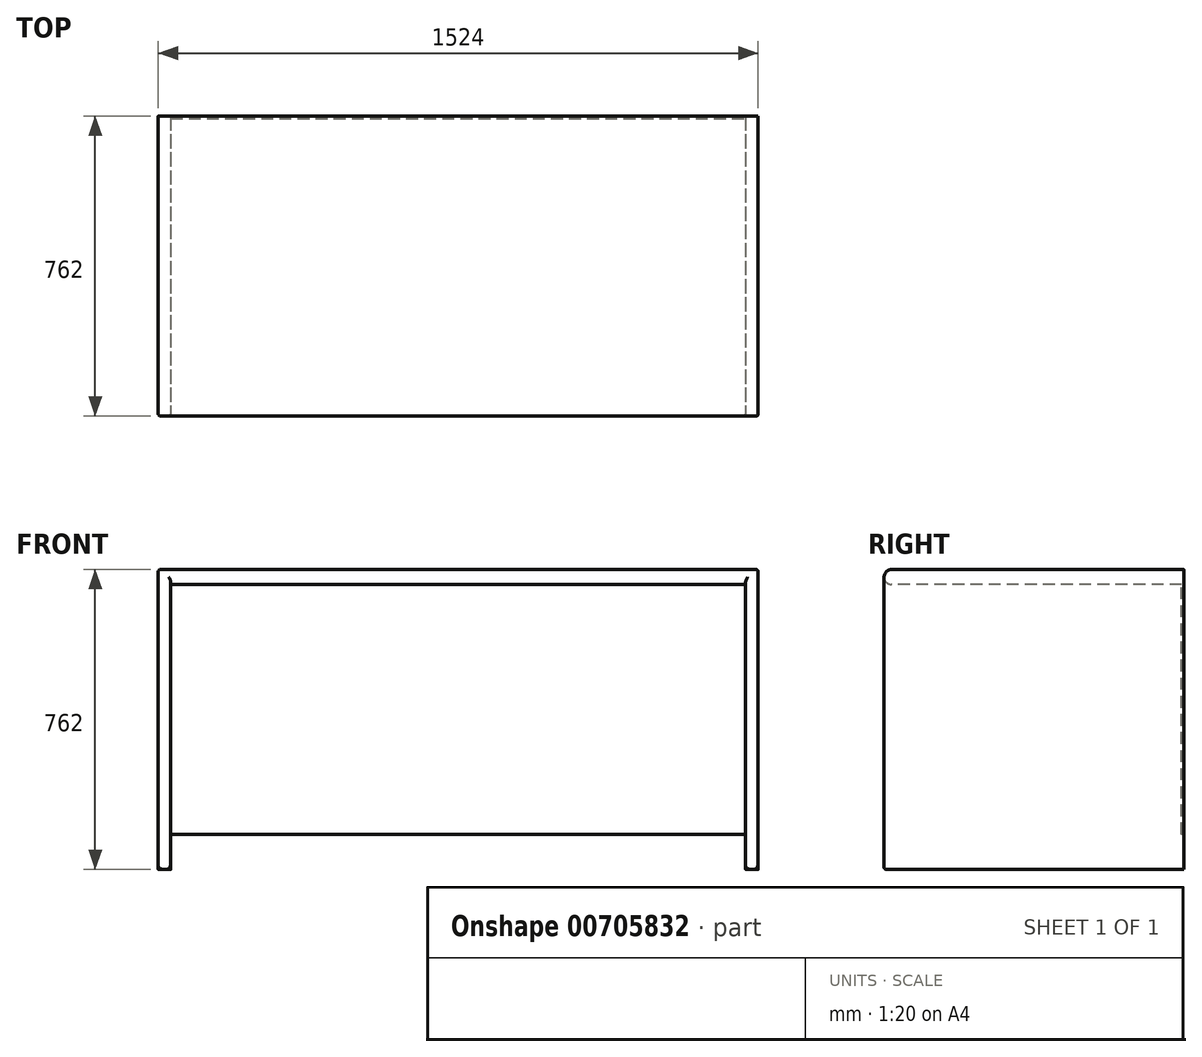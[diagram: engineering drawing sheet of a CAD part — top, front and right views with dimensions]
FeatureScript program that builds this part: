
annotation { "Feature Type Name" : "Feature", "Feature Type Description" : "" }
export const myFeature = defineFeature(function(context is Context, id is Id, definition is map)
    precondition{}
    {
        {
            var Q0;
            Q0=qCreatedBy(makeId("Top.planeOp"),FACE);
            var sketch = newSketch(context, id + "F0", { "sketchPlane" : qUnion([Q0])});
            skLineSegment(sketch, "E0.bottom", {"start": v(0, 0) * mm, "end": v(1524, 0) * mm});
            skLineSegment(sketch, "E0.top", {"start": v(0, 762) * mm, "end": v(1524, 762) * mm});
            skLineSegment(sketch, "E0.left", {"start": v(0, 0) * mm, "end": v(0, 762) * mm});
            skLineSegment(sketch, "E0.right", {"start": v(1524, 0) * mm, "end": v(1524, 762) * mm});
            skLineSegment(sketch, "E1", {"start": v(31.75, 762) * mm, "end": v(31.75, 0) * mm});
            skLineSegment(sketch, "E2", {"start": v(1492.25, 762) * mm, "end": v(1492.25, 0) * mm});
            skLineSegment(sketch, "E3", {"start": v(31.75, 755.65) * mm, "end": v(1492.25, 755.65) * mm});
            skSolve(sketch);
        }
        {
            var Q0;
            {var subQ5=sQuery(id+"F0.wireOp",EDGE,"E3");Q0=makeQuery(id+"F0.imprint","IMPRINT",FACE,{"disambiguationData":[TD([[makeQuery(id+"F0.imprint","IMPRINT",EDGE,{"derivedFrom":subQ5}),-1.0]])]});}
            var Q1;
            {var subQ0=sQuery(id+"F0.wireOp",EDGE,"E0.left");Q1=makeQuery(id+"F0.imprint","IMPRINT",FACE,{"disambiguationData":[TD([[makeQuery(id+"F0.imprint","IMPRINT",EDGE,{"derivedFrom":subQ0}),-1.0]])]});}
            var Q2;
            {var subQ5=sQuery(id+"F0.wireOp",EDGE,"E3");Q2=makeQuery(id+"F0.imprint","IMPRINT",FACE,{"disambiguationData":[TD([[makeQuery(id+"F0.imprint","IMPRINT",EDGE,{"derivedFrom":subQ5}),1.0]])]});}
            var Q3;
            {var subQ4=sQuery(id+"F0.wireOp",EDGE,"E0.right");Q3=makeQuery(id+"F0.imprint","IMPRINT",FACE,{"disambiguationData":[TD([[makeQuery(id+"F0.imprint","IMPRINT",EDGE,{"derivedFrom":subQ4}),1.0]])]});}
            extrude(context, id + "F1", {"entities" : qUnion([Q0, Q1, Q2, Q3]), "depth" : 38.1 * mm, "offsetDistance" : 25.4 * mm});
        }
        {
            var Q0;
            {var subQ0=sQuery(id+"F0.wireOp",EDGE,"E0.left");Q0=makeQuery(id+"F0.imprint","IMPRINT",FACE,{"disambiguationData":[TD([[makeQuery(id+"F0.imprint","IMPRINT",EDGE,{"derivedFrom":subQ0}),-1.0]])]});}
            var Q1;
            {var subQ4=sQuery(id+"F0.wireOp",EDGE,"E0.right");Q1=makeQuery(id+"F0.imprint","IMPRINT",FACE,{"disambiguationData":[TD([[makeQuery(id+"F0.imprint","IMPRINT",EDGE,{"derivedFrom":subQ4}),1.0]])]});}
            extrude(context, id + "F2", {"entities" : qUnion([Q0, Q1]), "operationType" : NewBodyOperationType.ADD, "oppositeDirection" : true, "depth" : 723.9 * mm, "offsetDistance" : 25.4 * mm});
        }
        {
            var Q0;
            {var subQ5=sQuery(id+"F0.wireOp",EDGE,"E3");Q0=makeQuery(id+"F0.imprint","IMPRINT",FACE,{"disambiguationData":[TD([[makeQuery(id+"F0.imprint","IMPRINT",EDGE,{"derivedFrom":subQ5}),1.0]])]});}
            extrude(context, id + "F3", {"entities" : qUnion([Q0]), "operationType" : NewBodyOperationType.ADD, "oppositeDirection" : true, "depth" : 635 * mm, "offsetDistance" : 25.4 * mm});
        }
        {
            var Q0;
            Q0=makeQuery(id+"F1.opExtrude","CAP_EDGE",EDGE,{"disambiguationData":[OSD([sQuery(id+"F0.wireOp",EDGE,"E0.bottom")])],"isStart":false});
            var Q1;
            Q1=makeQuery(id+"F1.opExtrude","CAP_EDGE",EDGE,{"disambiguationData":[OSD([sQuery(id+"F0.wireOp",EDGE,"E0.bottom")])],"isStart":true});
            fillet(context, id + "F4", {"entities" : qUnion([Q0, Q1]), "radius" : 19.05 * mm, "tangentPropagation" : true, "allowEdgeOverflow" : false});
        }
        {
            var Q0;
            {var subQ0=sQuery(id+"F0.wireOp",EDGE,"E0.bottom");Q0=makeQuery(id+"F4.opFillet","SPLIT",FACE,{"disambiguationData":[OD(0.0)],"derivedFrom":makeQuery(id+"F2.boolean.opBoolean","MERGE",FACE,{"derivedFrom":[makeQuery(id+"F1.opExtrude","SWEPT_FACE",FACE,{"disambiguationData":[OSD([subQ0])]}),makeQuery(id+"F2.opExtrude","SWEPT_FACE",FACE,{"disambiguationData":[OSD([subQ0]),TDD([makeQuery(id+"F0.imprint","IMPRINT",EDGE,{"disambiguationData":[TD([[makeQuery(id+"F0.imprint","INTERSECT",VERTEX,{"derivedFrom":[subQ0,sQuery(id+"F0.wireOp",EDGE,"E0.left")]}),-1.0]])],"derivedFrom":subQ0})])]}),makeQuery(id+"F2.opExtrude","SWEPT_FACE",FACE,{"disambiguationData":[OSD([subQ0]),TDD([makeQuery(id+"F0.imprint","IMPRINT",EDGE,{"disambiguationData":[TD([[makeQuery(id+"F0.imprint","INTERSECT",VERTEX,{"derivedFrom":[subQ0,sQuery(id+"F0.wireOp",EDGE,"E0.right")]}),1.0]])],"derivedFrom":subQ0})])]})]})});}
            var Q1;
            {var subQ0=sQuery(id+"F0.wireOp",EDGE,"E0.bottom");Q1=makeQuery(id+"F4.opFillet","SPLIT",FACE,{"disambiguationData":[OD(1.0)],"derivedFrom":makeQuery(id+"F2.boolean.opBoolean","MERGE",FACE,{"derivedFrom":[makeQuery(id+"F1.opExtrude","SWEPT_FACE",FACE,{"disambiguationData":[OSD([subQ0])]}),makeQuery(id+"F2.opExtrude","SWEPT_FACE",FACE,{"disambiguationData":[OSD([subQ0]),TDD([makeQuery(id+"F0.imprint","IMPRINT",EDGE,{"disambiguationData":[TD([[makeQuery(id+"F0.imprint","INTERSECT",VERTEX,{"derivedFrom":[subQ0,sQuery(id+"F0.wireOp",EDGE,"E0.left")]}),-1.0]])],"derivedFrom":subQ0})])]}),makeQuery(id+"F2.opExtrude","SWEPT_FACE",FACE,{"disambiguationData":[OSD([subQ0]),TDD([makeQuery(id+"F0.imprint","IMPRINT",EDGE,{"disambiguationData":[TD([[makeQuery(id+"F0.imprint","INTERSECT",VERTEX,{"derivedFrom":[subQ0,sQuery(id+"F0.wireOp",EDGE,"E0.right")]}),1.0]])],"derivedFrom":subQ0})])]})]})});}
            fillet(context, id + "F5", {"entities" : qUnion([Q0, Q1]), "radius" : 5.08 * mm, "tangentPropagation" : true, "allowEdgeOverflow" : false});
        }
    });
